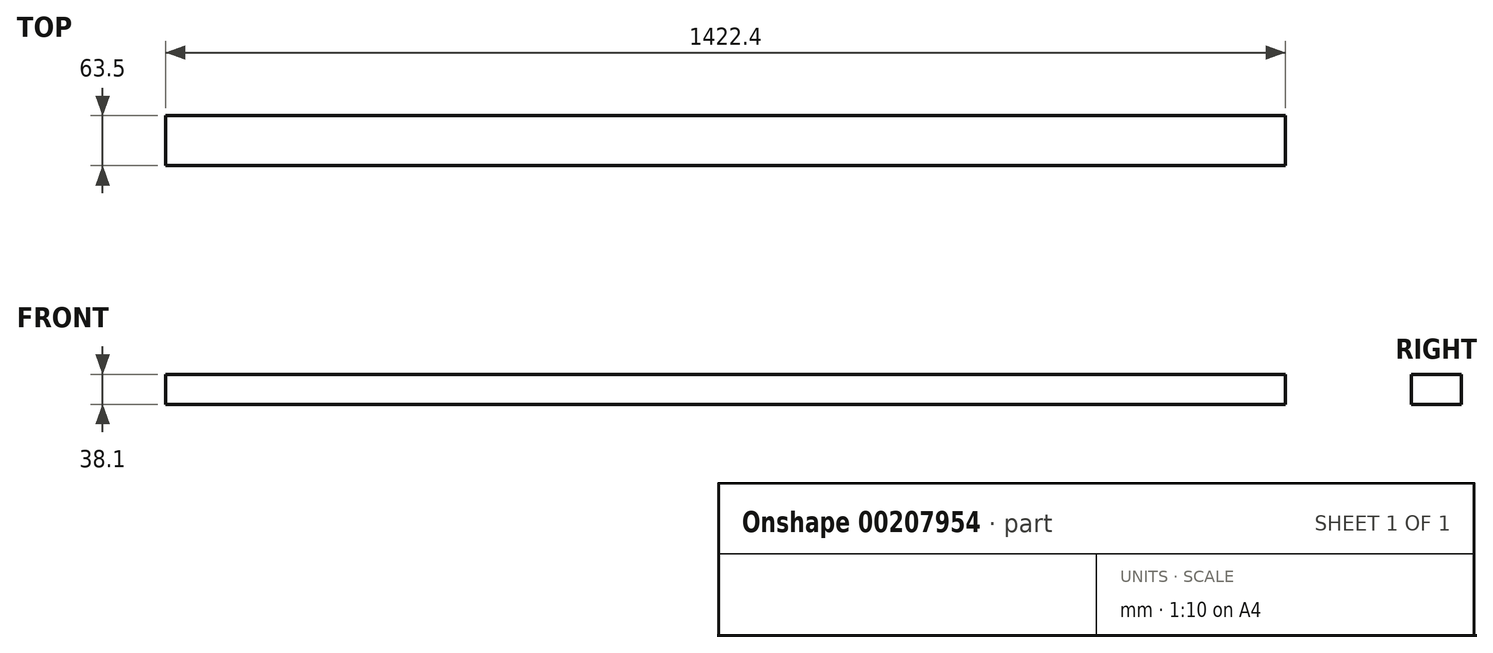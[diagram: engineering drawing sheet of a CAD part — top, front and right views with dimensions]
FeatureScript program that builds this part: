
annotation { "Feature Type Name" : "Feature", "Feature Type Description" : "" }
export const myFeature = defineFeature(function(context is Context, id is Id, definition is map)
    precondition{}
    {
        {
            var Q0;
            Q0=qCreatedBy(makeId("Right.planeOp"),FACE);
            var sketch = newSketch(context, id + "F0", { "sketchPlane" : qUnion([Q0])});
            skLineSegment(sketch, "E0.bottom", {"start": v(0, 0) * mm, "end": v(63.5, 0) * mm});
            skLineSegment(sketch, "E0.top", {"start": v(0, 38.1) * mm, "end": v(63.5, 38.1) * mm});
            skLineSegment(sketch, "E0.left", {"start": v(0, 0) * mm, "end": v(0, 38.1) * mm});
            skLineSegment(sketch, "E0.right", {"start": v(63.5, 0) * mm, "end": v(63.5, 38.1) * mm});
            skSolve(sketch);
        }
        {
            var Q0;
            Q0 = qSketchRegion(id + "F0", true);
            extrude(context, id + "F1", {"entities" : qUnion([Q0]), "depth" : 1422.4 * mm});
        }
    });
